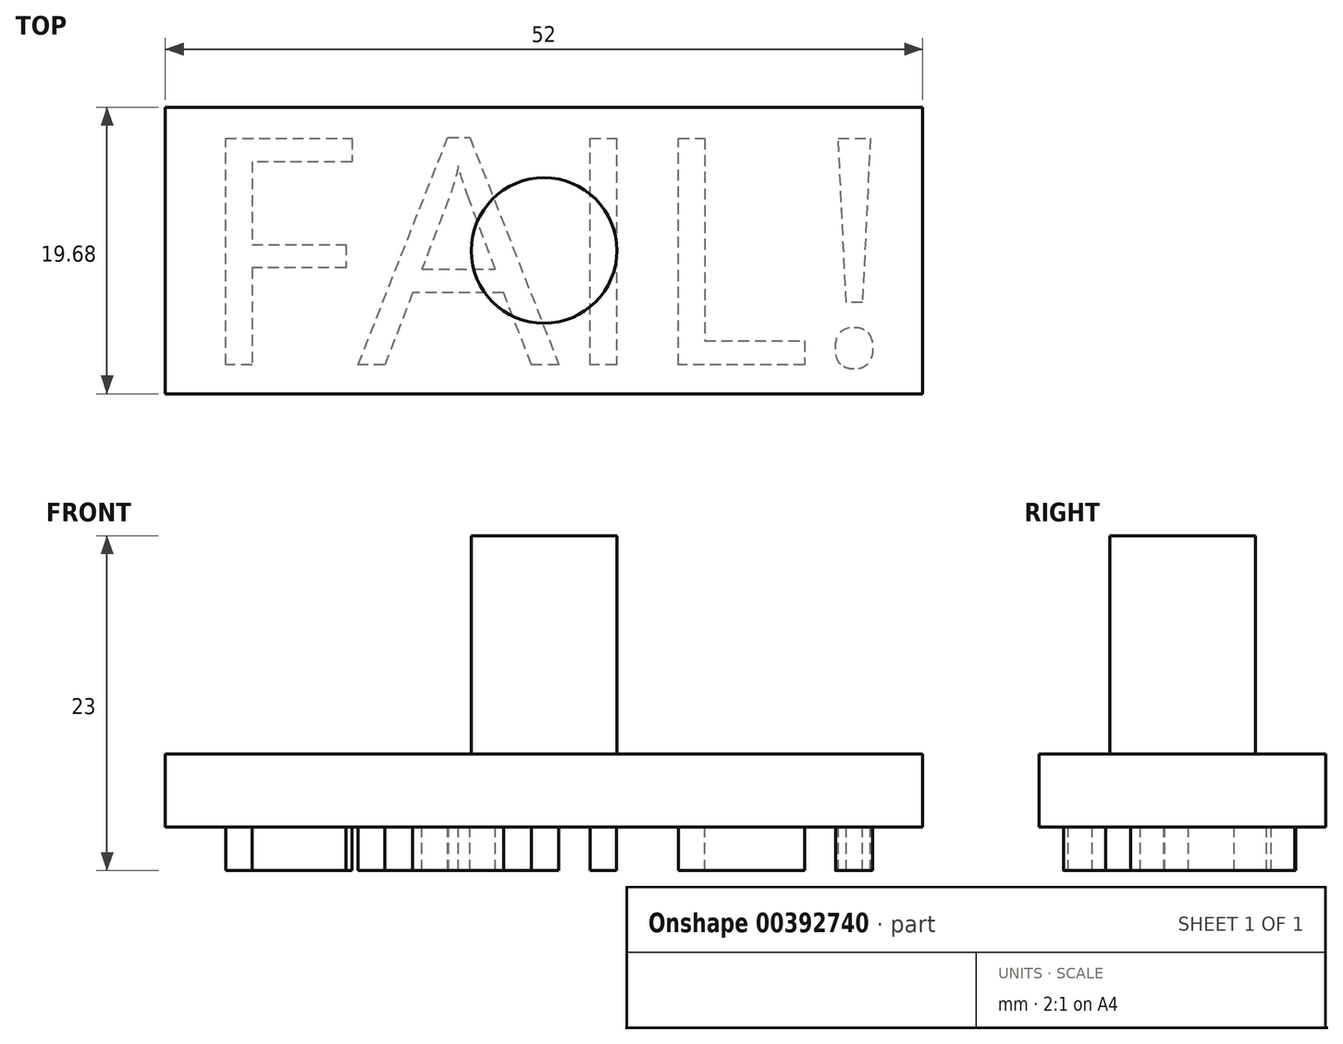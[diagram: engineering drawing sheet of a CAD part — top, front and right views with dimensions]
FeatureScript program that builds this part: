
annotation { "Feature Type Name" : "Feature", "Feature Type Description" : "" }
export const myFeature = defineFeature(function(context is Context, id is Id, definition is map)
    precondition{}
    {
        {
            var Q0;
            Q0=qCreatedBy(makeId("Top.planeOp"),FACE);
            var sketch = newSketch(context, id + "F0", { "sketchPlane" : qUnion([Q0])});
            skLineSegment(sketch, "E0.bottom", {"start": v(-26, -9.84) * mm, "end": v(26, -9.84) * mm});
            skLineSegment(sketch, "E0.top", {"start": v(-26, 9.84) * mm, "end": v(26, 9.84) * mm});
            skLineSegment(sketch, "E0.left", {"start": v(-26, -9.84) * mm, "end": v(-26, 9.84) * mm});
            skLineSegment(sketch, "E0.right", {"start": v(26, -9.84) * mm, "end": v(26, 9.84) * mm});
            skPoint(sketch, "E0.middle", {"position": v(0, 0) * mm});
            skText(sketch, "E1", { "text": "FAIL!", "fontName": "OpenSans-Regular.ttf"});
            skLineSegment(sketch, "E2", {"start": v(24, 7.84) * mm, "end": v(-24, -7.84) * mm, "construction": true});
            skLineSegment(sketch, "E3", {"start": v(-24, 7.84) * mm, "end": v(24, -7.84) * mm, "construction": true});
            const initialGuessF0  = {"E1": [-0.024, -0.00784, 1, 0, 0.01568]};
            skSetInitialGuess(sketch, initialGuessF0);
            skSolve(sketch);
        }
        {
            var Q0;
            Q0=makeQuery(id+"F0.imprint","IMPRINT",FACE,{"disambiguationData":[TD([[makeQuery(id+"F0.imprint","IMPRINT",EDGE,{"derivedFrom":sQuery(id+"F0.wireOp",EDGE,"E1.sketch_text.stroke-18")}),1.0]])]});
            var Q1;
            Q1 = qSketchRegion(id + "F0", true);
            var Q2;
            Q2=makeQuery(id+"F0.imprint","IMPRINT",FACE,{"disambiguationData":[TD([[makeQuery(id+"F0.imprint","IMPRINT",EDGE,{"derivedFrom":sQuery(id+"F0.wireOp",EDGE,"E1.sketch_text.stroke-0")}),-1.0]])]});
            var Q3;
            Q3=makeQuery(id+"F0.imprint","IMPRINT",FACE,{"disambiguationData":[TD([[makeQuery(id+"F0.imprint","IMPRINT",EDGE,{"derivedFrom":sQuery(id+"F0.wireOp",EDGE,"E1.sketch_text.stroke-10")}),-1.0]])]});
            var Q4;
            Q4=makeQuery(id+"F0.imprint","IMPRINT",FACE,{"disambiguationData":[TD([[makeQuery(id+"F0.imprint","IMPRINT",EDGE,{"derivedFrom":sQuery(id+"F0.wireOp",EDGE,"E0.bottom")}),1.0]])]});
            var Q5;
            Q5=makeQuery(id+"F0.imprint","IMPRINT",FACE,{"disambiguationData":[TD([[makeQuery(id+"F0.imprint","IMPRINT",EDGE,{"derivedFrom":sQuery(id+"F0.wireOp",EDGE,"E1.sketch_text.stroke-23")}),-1.0]])]});
            var Q6;
            Q6=makeQuery(id+"F0.imprint","IMPRINT",FACE,{"disambiguationData":[TD([[makeQuery(id+"F0.imprint","IMPRINT",EDGE,{"derivedFrom":sQuery(id+"F0.wireOp",EDGE,"E1.sketch_text.stroke-27")}),-1.0]])]});
            var Q7;
            Q7=makeQuery(id+"F0.imprint","IMPRINT",FACE,{"disambiguationData":[TD([[makeQuery(id+"F0.imprint","IMPRINT",EDGE,{"derivedFrom":sQuery(id+"F0.wireOp",EDGE,"E1.sketch_text.stroke-33")}),-1.0]])]});
            var Q8;
            Q8=makeQuery(id+"F0.imprint","IMPRINT",FACE,{"disambiguationData":[TD([[makeQuery(id+"F0.imprint","IMPRINT",EDGE,{"derivedFrom":sQuery(id+"F0.wireOp",EDGE,"E1.sketch_text.stroke-37")}),-1.0]])]});
            extrude(context, id + "F1", {"entities" : qUnion([Q0, Q1, Q2, Q3, Q4, Q5, Q6, Q7, Q8]), "depth" : 5 * mm});
        }
        {
            var Q0;
            Q0=makeQuery(id+"F0.imprint","IMPRINT",FACE,{"disambiguationData":[TD([[makeQuery(id+"F0.imprint","IMPRINT",EDGE,{"derivedFrom":sQuery(id+"F0.wireOp",EDGE,"E1.sketch_text.stroke-0")}),-1.0]])]});
            var Q1;
            Q1=makeQuery(id+"F0.imprint","IMPRINT",FACE,{"disambiguationData":[TD([[makeQuery(id+"F0.imprint","IMPRINT",EDGE,{"derivedFrom":sQuery(id+"F0.wireOp",EDGE,"E1.sketch_text.stroke-10")}),-1.0]])]});
            var Q2;
            Q2=makeQuery(id+"F0.imprint","IMPRINT",FACE,{"disambiguationData":[TD([[makeQuery(id+"F0.imprint","IMPRINT",EDGE,{"derivedFrom":sQuery(id+"F0.wireOp",EDGE,"E1.sketch_text.stroke-23")}),-1.0]])]});
            var Q3;
            Q3=makeQuery(id+"F0.imprint","IMPRINT",FACE,{"disambiguationData":[TD([[makeQuery(id+"F0.imprint","IMPRINT",EDGE,{"derivedFrom":sQuery(id+"F0.wireOp",EDGE,"E1.sketch_text.stroke-27")}),-1.0]])]});
            var Q4;
            Q4=makeQuery(id+"F0.imprint","IMPRINT",FACE,{"disambiguationData":[TD([[makeQuery(id+"F0.imprint","IMPRINT",EDGE,{"derivedFrom":sQuery(id+"F0.wireOp",EDGE,"E1.sketch_text.stroke-37")}),-1.0]])]});
            var Q5;
            Q5=makeQuery(id+"F0.imprint","IMPRINT",FACE,{"disambiguationData":[TD([[makeQuery(id+"F0.imprint","IMPRINT",EDGE,{"derivedFrom":sQuery(id+"F0.wireOp",EDGE,"E1.sketch_text.stroke-33")}),-1.0]])]});
            extrude(context, id + "F2", {"entities" : qUnion([Q0, Q1, Q2, Q3, Q4, Q5]), "operationType" : NewBodyOperationType.ADD, "depth" : -3 * mm});
        }
        {
            var Q0;
            Q0=makeQuery(id+"F1.opExtrude","CAP_FACE",FACE,{"disambiguationData":[OSD([sQuery(id+"F0.wireOp",EDGE,"E0.bottom"),sQuery(id+"F0.wireOp",EDGE,"E0.top"),sQuery(id+"F0.wireOp",EDGE,"E0.left"),sQuery(id+"F0.wireOp",EDGE,"E0.right")])],"isStart":false});
            var sketch = newSketch(context, id + "F3", { "sketchPlane" : qUnion([Q0])});
            skCircle(sketch, "E4", {"center": v(0, 0) * mm, "radius": 5 * mm});
            skSolve(sketch);
        }
        {
            var Q0;
            Q0=makeQuery(id+"F3.imprint","IMPRINT",FACE,{"disambiguationData":[TD([[makeQuery(id+"F3.imprint","IMPRINT",EDGE,{"derivedFrom":sQuery(id+"F3.wireOp",EDGE,"E4")}),1.0]])]});
            extrude(context, id + "F4", {"entities" : qUnion([Q0]), "operationType" : NewBodyOperationType.ADD, "depth" : 15 * mm});
        }
    });
